# Revit family: ПР_18.01.2022
name_source: partatom
category: Оборудование
units: mm (PartAtom-declared; Revit-internal decimal feet)

## family parameters
Всегда вертикально = Да
Классификация = Нет
На основе рабочей плоскости = Нет
Общий = Нет
При загрузке вырезать с полостями = Нет
Размер круглого соединителя = Использовать диаметр
Тип детали = Нормальный
Точка расчета площади = Нет

## types (3) — shared parameters
Панель = Нет
светодиод RS-485 = Нет
текст RS-485 = Нет
текст ПУМ = Нет
текст ПУМ 4.2 = Нет
zero-valued in all types: Отметка по умолчанию

## per-type parameters (varying)
| type | светодиод RS-PR | светодиод RS-PUM | светодиод Питание | светодиод Прибор | текст RS-PR | текст RS-PR для ПР-10.5 | текст RS-PUM | текст ПР-10.5 | текст ПР-4.2 | текст Панель расширения | текст Питание | текст Прибор | текст Работа |
| Панель расширения | Нет | Да | Да | Нет | Нет | Нет | Да | Нет | Нет | Да | Да | Нет | Нет |
| Прибор расширения модификации 4.2 | Да | Нет | Нет | Да | Да | Нет | Нет | Нет | Да | Нет | Нет | Да | Нет |
| Панель расширения модификации 10.5 | Нет | Да | Да | Нет | Нет | Да | Нет | Да | Нет | Нет | Нет | Нет | Да |
